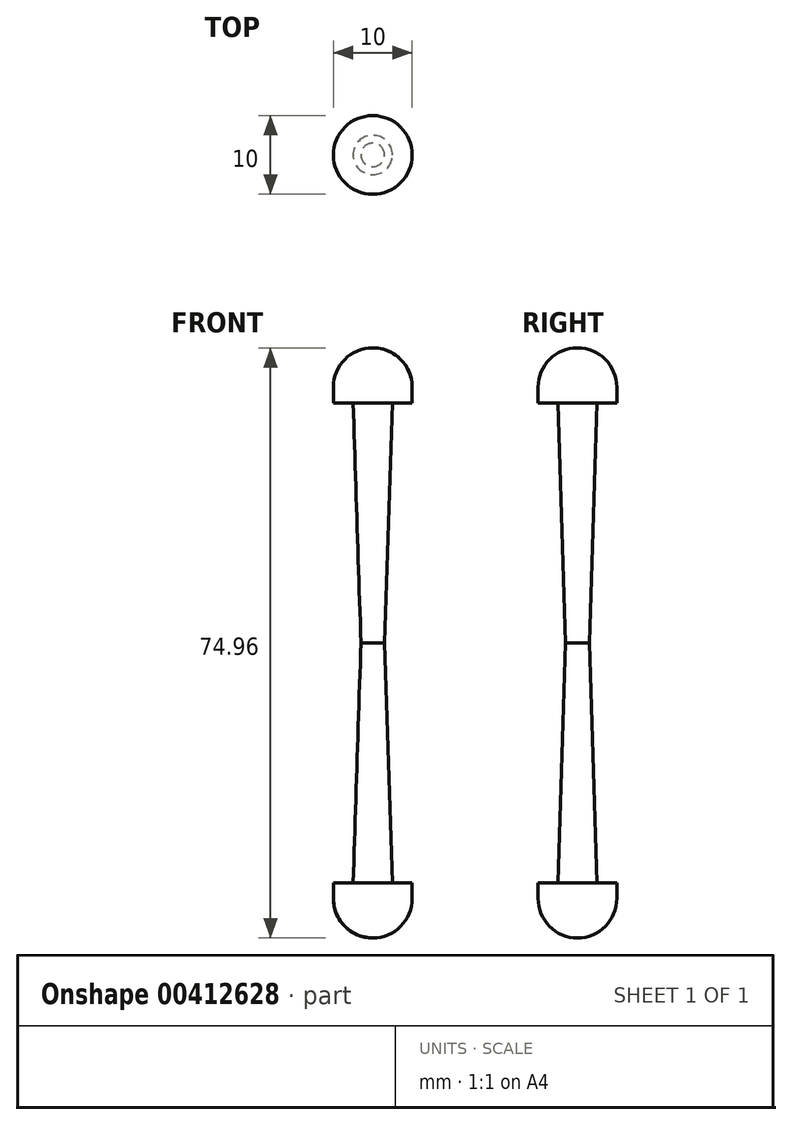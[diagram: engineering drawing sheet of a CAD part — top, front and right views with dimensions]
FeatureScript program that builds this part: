
annotation { "Feature Type Name" : "Feature", "Feature Type Description" : "" }
export const myFeature = defineFeature(function(context is Context, id is Id, definition is map)
    precondition{}
    {
        {
            var Q0;
            Q0=qCreatedBy(makeId("Front.planeOp"),FACE);
            var sketch = newSketch(context, id + "F0", { "sketchPlane" : qUnion([Q0])});
            skLineSegment(sketch, "E0", {"start": v(0, 0) * mm, "end": v(0, -32.48) * mm});
            skLineSegment(sketch, "E1", {"start": v(0, -32.48) * mm, "end": v(5, -32.48) * mm});
            skLineSegment(sketch, "E2", {"start": v(5, -32.48) * mm, "end": v(5, -30.48) * mm});
            skLineSegment(sketch, "E3", {"start": v(5, -30.48) * mm, "end": v(2.5, -30.48) * mm});
            skLineSegment(sketch, "E4", {"start": v(2.5, -30.48) * mm, "end": v(1.5, 0) * mm});
            skLineSegment(sketch, "E5.MirrorCS", {"start": v(5, 30.48) * mm, "end": v(2.5, 30.48) * mm});
            skLineSegment(sketch, "E6.MirrorCS", {"start": v(0, 32.48) * mm, "end": v(5, 32.48) * mm});
            skLineSegment(sketch, "E7.MirrorCS", {"start": v(5, 32.48) * mm, "end": v(5, 30.48) * mm});
            skLineSegment(sketch, "E8.MirrorCS", {"start": v(2.5, 30.48) * mm, "end": v(1.5, 0) * mm});
            skLineSegment(sketch, "E9.MirrorCS", {"start": v(0, 0) * mm, "end": v(0, 32.48) * mm});
            skArc(sketch, "E10", {"start": v(0, -37.48) * mm, "mid": v(3.54, -36.02) * mm, "end": v(5, -32.48) * mm});
            skLineSegment(sketch, "E11", {"start": v(0, -32.48) * mm, "end": v(0, -37.48) * mm});
            skArc(sketch, "E12.MirrorCS", {"start": v(0, 37.48) * mm, "mid": v(3.54, 36.02) * mm, "end": v(5, 32.48) * mm});
            skLineSegment(sketch, "E13", {"start": v(0, 37.48) * mm, "end": v(0, 32.48) * mm});
            skSolve(sketch);
        }
        {
            var Q0;
            Q0 = qSketchRegion(id + "F0", true);
            var Q1;
            Q1=sQuery(id+"F0.wireOp",EDGE,"E9.MirrorCS");
            revolve(context, id + "F1", {"entities" : qUnion([Q0]), "axis" : qUnion([Q1]), "revolveType" : RevolveType.FULL});
        }
    });
